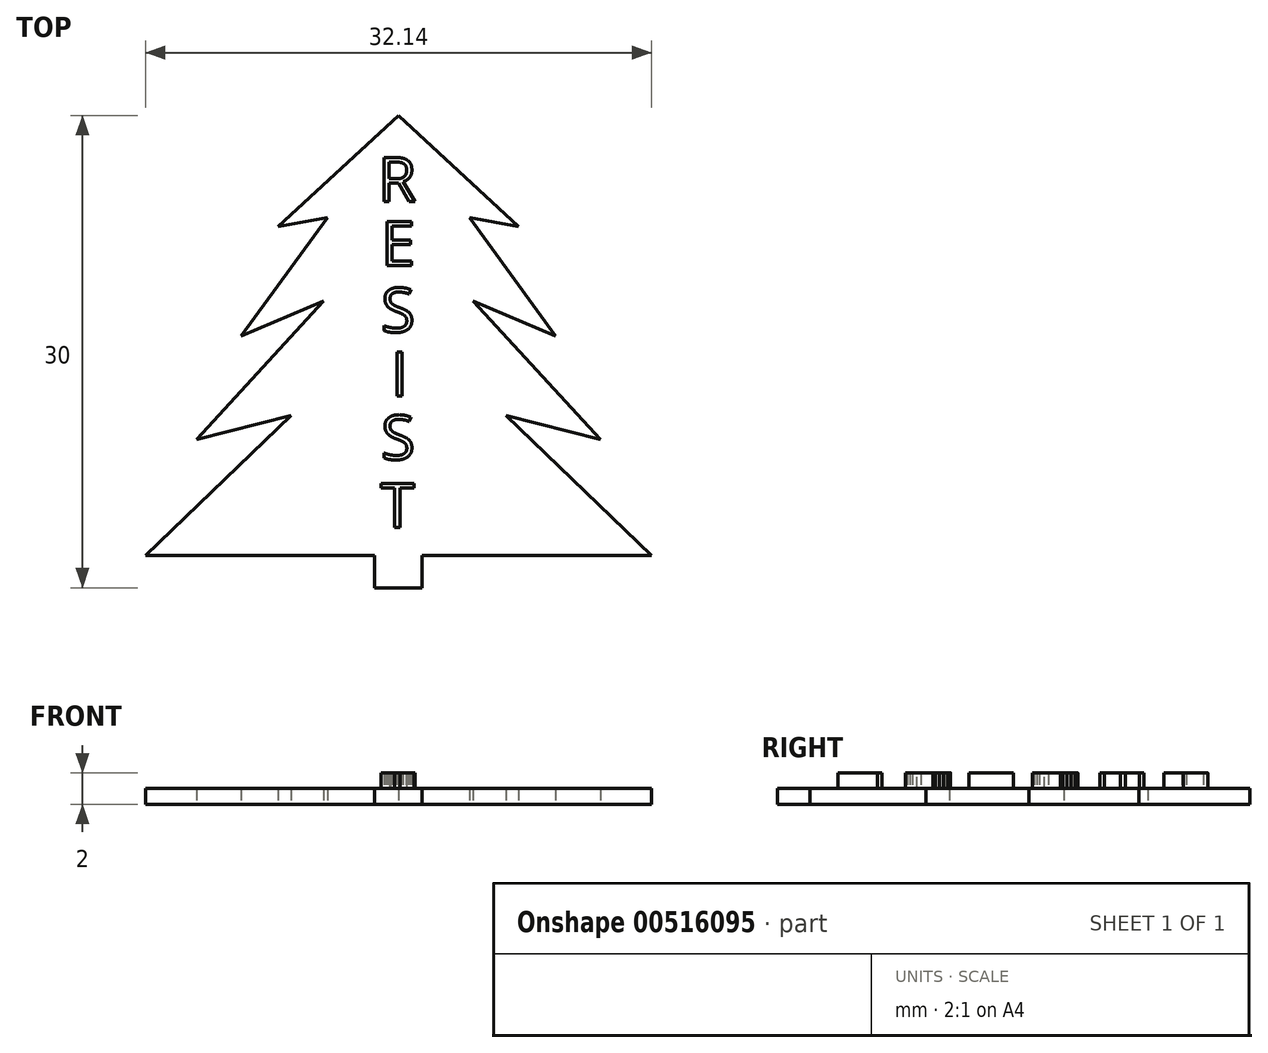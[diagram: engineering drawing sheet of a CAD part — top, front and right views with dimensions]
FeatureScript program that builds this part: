
annotation { "Feature Type Name" : "Feature", "Feature Type Description" : "" }
export const myFeature = defineFeature(function(context is Context, id is Id, definition is map)
    precondition{}
    {
        {
            var Q0;
            Q0=qCreatedBy(makeId("Top.planeOp"),FACE);
            var sketch = newSketch(context, id + "F0", { "sketchPlane" : qUnion([Q0])});
            skLineSegment(sketch, "E0", {"start": v(0, 30) * mm, "end": v(-7.63, 22.95) * mm});
            skLineSegment(sketch, "E1", {"start": v(-13.72, 2.06) * mm, "end": v(-1.5, 2.06) * mm});
            skLineSegment(sketch, "E2", {"start": v(-1.5, 2.06) * mm, "end": v(-1.5, 0) * mm});
            skLineSegment(sketch, "E3", {"start": v(-1.5, 0) * mm, "end": v(0, 0) * mm});
            skLineSegment(sketch, "E4", {"start": v(-4.51, 23.53) * mm, "end": v(-9.98, 15.99) * mm});
            skLineSegment(sketch, "E5", {"start": v(0, 0) * mm, "end": v(0, 30) * mm, "construction": true});
            skLineSegment(sketch, "E6.MirrorCS", {"start": v(0, 30) * mm, "end": v(7.63, 22.95) * mm});
            skLineSegment(sketch, "E7.MirrorCS", {"start": v(4.51, 23.53) * mm, "end": v(9.98, 15.99) * mm});
            skLineSegment(sketch, "E8.MirrorCS", {"start": v(13.72, 2.06) * mm, "end": v(1.5, 2.06) * mm});
            skLineSegment(sketch, "E9.MirrorCS", {"start": v(1.5, 0) * mm, "end": v(0, 0) * mm});
            skLineSegment(sketch, "E10.MirrorCS", {"start": v(1.5, 2.06) * mm, "end": v(1.5, 0) * mm});
            skLineSegment(sketch, "E11", {"start": v(-7.63, 22.95) * mm, "end": v(-4.51, 23.53) * mm});
            skLineSegment(sketch, "E12", {"start": v(4.51, 23.53) * mm, "end": v(7.63, 22.95) * mm});
            skLineSegment(sketch, "E13", {"start": v(-9.98, 15.99) * mm, "end": v(-4.74, 18.21) * mm});
            skLineSegment(sketch, "E14", {"start": v(-4.74, 18.21) * mm, "end": v(-12.83, 9.43) * mm});
            skLineSegment(sketch, "E15", {"start": v(-12.83, 9.43) * mm, "end": v(-6.82, 10.93) * mm});
            skLineSegment(sketch, "E16", {"start": v(-6.82, 10.93) * mm, "end": v(-16.07, 2.06) * mm});
            skLineSegment(sketch, "E17", {"start": v(-16.07, 2.06) * mm, "end": v(-13.72, 2.06) * mm});
            skLineSegment(sketch, "E18.MirrorCS", {"start": v(6.82, 10.93) * mm, "end": v(16.07, 2.06) * mm});
            skLineSegment(sketch, "E19.MirrorCS", {"start": v(12.83, 9.43) * mm, "end": v(6.82, 10.93) * mm});
            skLineSegment(sketch, "E20.MirrorCS", {"start": v(4.74, 18.21) * mm, "end": v(12.83, 9.43) * mm});
            skLineSegment(sketch, "E21.MirrorCS", {"start": v(9.98, 15.99) * mm, "end": v(4.74, 18.21) * mm});
            skLineSegment(sketch, "E22.MirrorCS", {"start": v(16.07, 2.06) * mm, "end": v(13.72, 2.06) * mm});
            skSolve(sketch);
        }
        {
            var Q0;
            Q0=makeQuery(id+"F0.imprint","IMPRINT",FACE,{"disambiguationData":[TD([[makeQuery(id+"F0.imprint","IMPRINT",EDGE,{"derivedFrom":sQuery(id+"F0.wireOp",EDGE,"E0")}),1.0]])]});
            extrude(context, id + "F1", {"entities" : qUnion([Q0]), "depth" : 1 * mm, "offsetDistance" : 25 * mm});
        }
        {
            var Q0;
            Q0=makeQuery(id+"F1.opExtrude","CAP_FACE",FACE,{"disambiguationData":[OSD([sQuery(id+"F0.wireOp",EDGE,"E0"),sQuery(id+"F0.wireOp",EDGE,"E1"),sQuery(id+"F0.wireOp",EDGE,"E2"),sQuery(id+"F0.wireOp",EDGE,"E3"),sQuery(id+"F0.wireOp",EDGE,"E4"),sQuery(id+"F0.wireOp",EDGE,"E6.MirrorCS"),sQuery(id+"F0.wireOp",EDGE,"E7.MirrorCS"),sQuery(id+"F0.wireOp",EDGE,"E8.MirrorCS"),sQuery(id+"F0.wireOp",EDGE,"E9.MirrorCS"),sQuery(id+"F0.wireOp",EDGE,"E10.MirrorCS"),sQuery(id+"F0.wireOp",EDGE,"E11"),sQuery(id+"F0.wireOp",EDGE,"E12"),sQuery(id+"F0.wireOp",EDGE,"E13"),sQuery(id+"F0.wireOp",EDGE,"E14"),sQuery(id+"F0.wireOp",EDGE,"E15"),sQuery(id+"F0.wireOp",EDGE,"E16"),sQuery(id+"F0.wireOp",EDGE,"E17"),sQuery(id+"F0.wireOp",EDGE,"E18.MirrorCS"),sQuery(id+"F0.wireOp",EDGE,"E19.MirrorCS"),sQuery(id+"F0.wireOp",EDGE,"E20.MirrorCS"),sQuery(id+"F0.wireOp",EDGE,"E21.MirrorCS"),sQuery(id+"F0.wireOp",EDGE,"E22.MirrorCS")])],"isStart":false});
            var sketch = newSketch(context, id + "F2", { "sketchPlane" : qUnion([Q0])});
            skText(sketch, "E23", { "text": "R", "fontName": "OpenSans-Regular.ttf"});
            skText(sketch, "E24", { "text": "E", "fontName": "OpenSans-Regular.ttf"});
            skPoint(sketch, "E25.firstSnap0", {"position": v(-1.1, 21.88) * mm});
            skText(sketch, "E26", { "text": "I", "fontName": "OpenSans-Regular.ttf"});
            skText(sketch, "E27", { "text": "S", "fontName": "OpenSans-Regular.ttf"});
            skText(sketch, "E28", { "text": "T", "fontName": "OpenSans-Regular.ttf"});
            skLineSegment(sketch, "E29", {"start": v(0, 0) * mm, "end": v(0, 30) * mm, "construction": true});
            skText(sketch, "E30", { "text": "S", "fontName": "OpenSans-Regular.ttf"});
            const initialGuessF2  = {"E23": [-0.0013, 0.02454, 1, 0, 0.00282], "E24": [-0.0011, 0.02048, 1, 0, 0.00282], "E26": [-0.00048, 0.01218, 1, 0, 0.00282], "E27": [-0.0011, 0.01625, 1, 0, 0.00282], "E28": [-0.00115, 0.00384, 1, 0, 0.00282], "E30": [-0.0011, 0.00816, 1, 0, 0.00282]};
            skSetInitialGuess(sketch, initialGuessF2);
            skSolve(sketch);
        }
        {
            var Q0;
            Q0=qSketchRegion(id+"F2",true);
            extrude(context, id + "F3", {"entities" : qUnion([Q0]), "operationType" : NewBodyOperationType.ADD, "depth" : 1 * mm, "offsetDistance" : 25 * mm});
        }
    });
